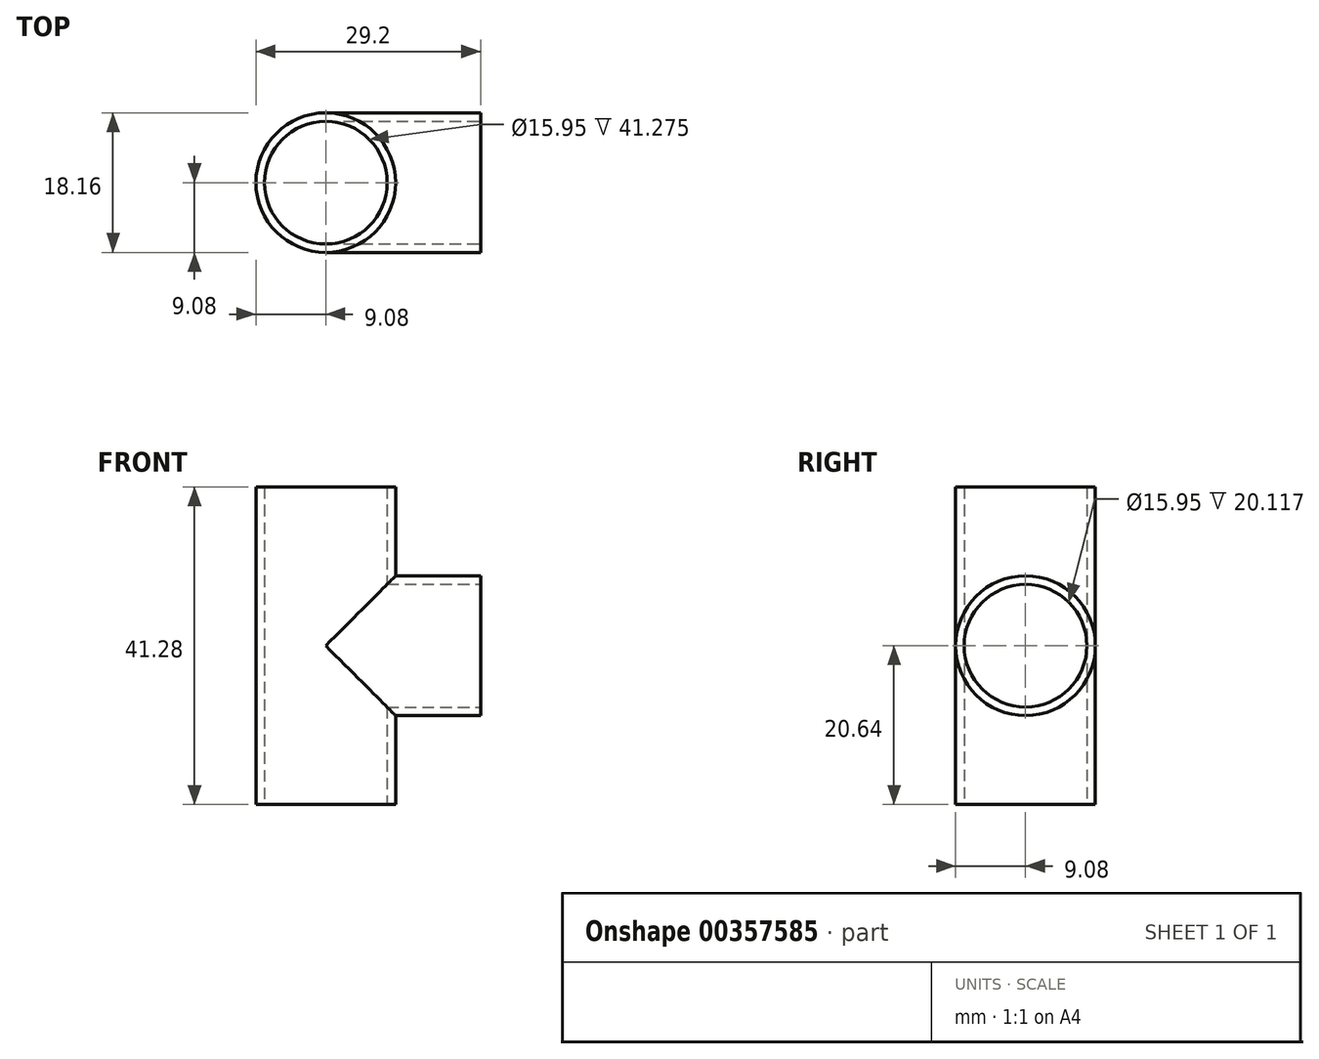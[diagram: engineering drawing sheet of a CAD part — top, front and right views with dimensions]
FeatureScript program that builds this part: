
annotation { "Feature Type Name" : "Feature", "Feature Type Description" : "" }
export const myFeature = defineFeature(function(context is Context, id is Id, definition is map)
    precondition{}
    {
        {
            var Q0;
            Q0=qCreatedBy(makeId("Top.planeOp"),FACE);
            var sketch = newSketch(context, id + "F0", { "sketchPlane" : qUnion([Q0])});
            skCircle(sketch, "E0", {"center": v(0, 0) * mm, "radius": 7.98 * mm});
            skCircle(sketch, "E1", {"center": v(0, 0) * mm, "radius": 9.08 * mm});
            skSolve(sketch);
        }
        {
            var Q0;
            Q0=makeQuery(id+"F0.imprint","IMPRINT",FACE,{"disambiguationData":[TD([[makeQuery(id+"F0.imprint","IMPRINT",EDGE,{"derivedFrom":sQuery(id+"F0.wireOp",EDGE,"E0")}),-1.0]])]});
            extrude(context, id + "F1", {"entities" : qUnion([Q0]), "depth" : 41.27 * mm, "symmetric" : true});
        }
        {
            var Q0;
            Q0=qCreatedBy(makeId("Front.planeOp"),FACE);
            var sketch = newSketch(context, id + "F2", { "sketchPlane" : qUnion([Q0])});
            skPoint(sketch, "E2", {"position": v(20.12, 0) * mm});
            skSolve(sketch);
        }
        {
            var Q0;
            Q0=qCreatedBy(makeId("Right.planeOp"),FACE);
            var Q1;
            Q1=sQuery(id+"F2.wireOp",VERTEX,"E2");
            cPlane(context, id + "F3", {"entities" : qUnion([Q0, Q1]), "cplaneType" : CPlaneType.PLANE_POINT, "offset" : 25.4 * mm, "width" : 152.4 * mm, "height" : 152.4 * mm});
        }
        {
            var Q0;
            Q0=qCreatedBy(id+"F3.planeOp",FACE);
            var sketch = newSketch(context, id + "F4", { "sketchPlane" : qUnion([Q0])});
            skLineSegment(sketch, "E3", {"start": v(-9.08, -20.64) * mm, "end": v(-9.08, 20.64) * mm, "construction": true});
            skCircle(sketch, "E4", {"center": v(0, 0) * mm, "radius": 9.08 * mm});
            skLineSegment(sketch, "E5.0", {"start": v(-7.98, 20.64) * mm, "end": v(7.98, 20.64) * mm, "construction": true});
            skLineSegment(sketch, "E6", {"start": v(-7.98, 20.64) * mm, "end": v(-7.98, -20.67) * mm, "construction": true});
            skCircle(sketch, "E7", {"center": v(0, 0) * mm, "radius": 7.98 * mm});
            skSolve(sketch);
        }
        {
            var Q0;
            Q0 = qSketchRegion(id + "F4", true);
            var Q1;
            Q1=makeQuery(id+"F1.opExtrude","SWEPT_FACE",FACE,{"disambiguationData":[OSD([sQuery(id+"F0.wireOp",EDGE,"E0")])]});
            var Q2;
            Q2=makeQuery(id+"F1.opExtrude","SWEPT_BODY",BODY,{"disambiguationData":[OSD([sQuery(id+"F0.wireOp",EDGE,"E0"),sQuery(id+"F0.wireOp",EDGE,"E1")])]});
            extrude(context, id + "F5", {"entities" : qUnion([Q0]), "operationType" : NewBodyOperationType.ADD, "endBound" : BoundingType.UP_TO_BODY, "oppositeDirection" : true, "endBoundEntityFace" : qUnion([Q1]), "endBoundEntityBody" : qUnion([Q2]), "depth" : 25.4 * mm});
        }
        {
            var Q0;
            Q0=qCreatedBy(id+"F3.planeOp",FACE);
            var sketch = newSketch(context, id + "F6", { "sketchPlane" : qUnion([Q0])});
            skCircle(sketch, "E8.0", {"center": v(0, 0) * mm, "radius": 7.98 * mm});
            skSolve(sketch);
        }
        {
            var Q0;
            Q0=makeQuery(id+"F6.imprint","IMPRINT",FACE,{"disambiguationData":[TD([[makeQuery(id+"F6.imprint","IMPRINT",EDGE,{"derivedFrom":sQuery(id+"F6.wireOp",EDGE,"E8.0")}),1.0]])]});
            var Q1;
            Q1=makeQuery(id+"F1.opExtrude","SWEPT_FACE",FACE,{"disambiguationData":[OSD([sQuery(id+"F0.wireOp",EDGE,"E0")])]});
            extrude(context, id + "F7", {"entities" : qUnion([Q0]), "operationType" : NewBodyOperationType.REMOVE, "endBound" : BoundingType.UP_TO_SURFACE, "oppositeDirection" : true, "endBoundEntityFace" : qUnion([Q1]), "depth" : 25.4 * mm});
        }
    });
